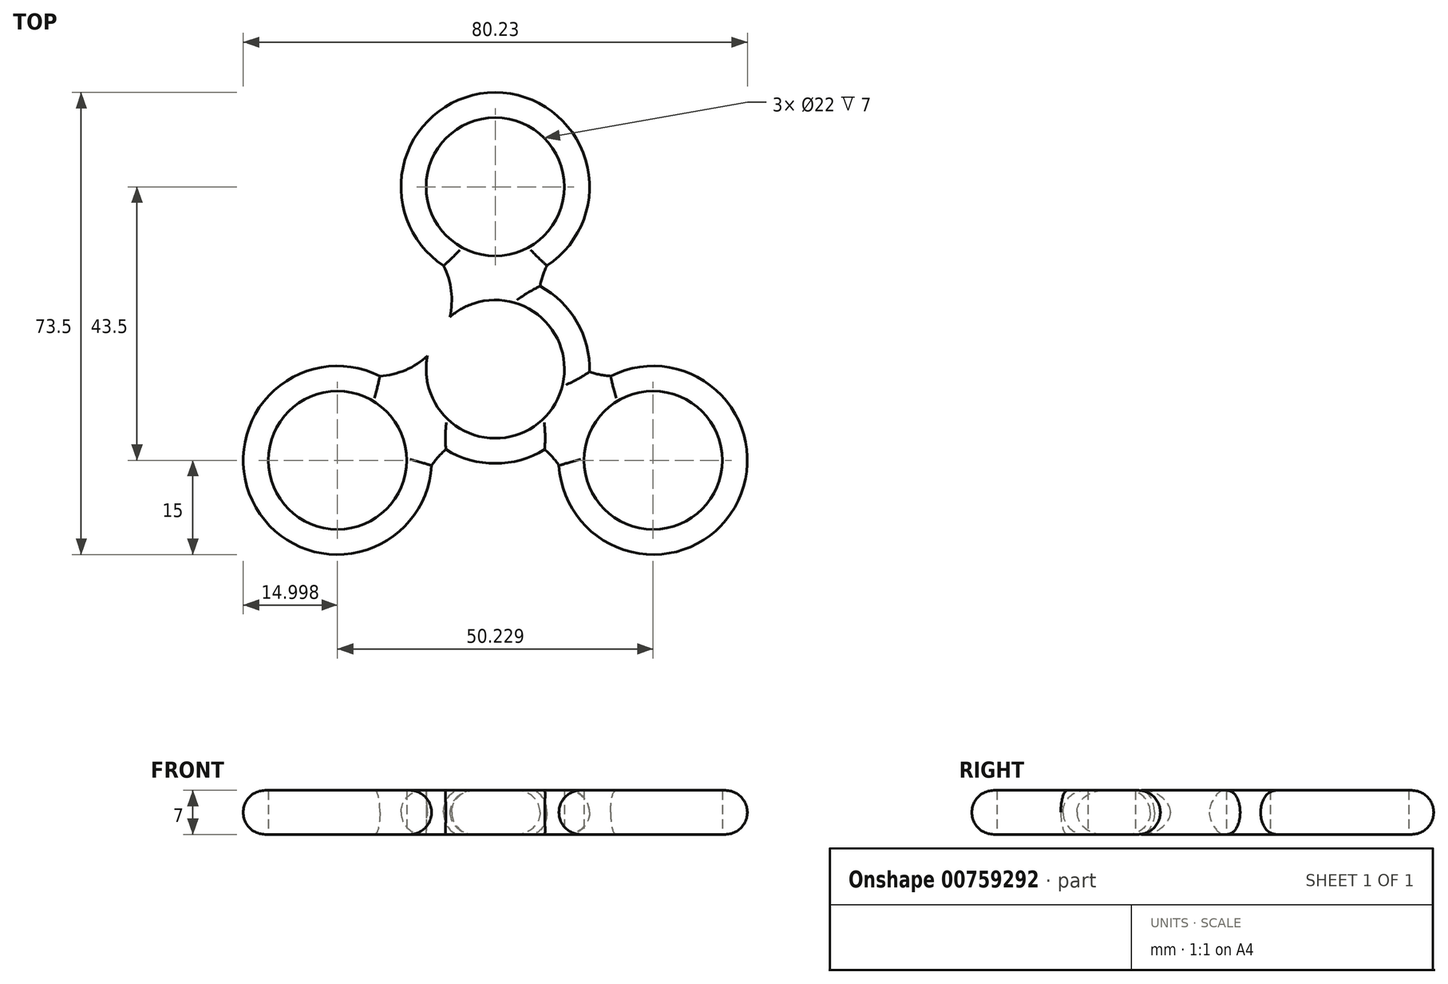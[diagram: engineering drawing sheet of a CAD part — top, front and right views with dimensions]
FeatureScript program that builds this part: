
annotation { "Feature Type Name" : "Feature", "Feature Type Description" : "" }
export const myFeature = defineFeature(function(context is Context, id is Id, definition is map)
    precondition{}
    {
        {
            var Q0;
            Q0=qCreatedBy(makeId("Top.planeOp"),FACE);
            var sketch = newSketch(context, id + "F0", { "sketchPlane" : qUnion([Q0])});
            skCircle(sketch, "E0", {"center": v(-46.13, 29) * mm, "radius": 15 * mm});
            skLineSegment(sketch, "E1", {"start": v(-46.13, 29) * mm, "end": v(-46.13, 0) * mm});
            skCircle(sketch, "E2.1.0", {"center": v(-71.24, -14.5) * mm, "radius": 15 * mm});
            skLineSegment(sketch, "E2.1.1", {"start": v(-71.24, -14.5) * mm, "end": v(-46.13, 0) * mm});
            skCircle(sketch, "E2.2.0", {"center": v(-21.01, -14.5) * mm, "radius": 15 * mm});
            skLineSegment(sketch, "E2.2.1", {"start": v(-21.01, -14.5) * mm, "end": v(-46.13, 0) * mm});
            skPoint(sketch, "E2.center", {"position": v(-46.13, 0) * mm});
            skLineSegment(sketch, "E3", {"start": v(-46.13, 29) * mm, "end": v(-59.12, 36.5) * mm});
            skLineSegment(sketch, "E4", {"start": v(-71.24, -14.5) * mm, "end": v(-84.23, -7) * mm});
            skPoint(sketch, "E5", {"position": v(-59.12, 21.5) * mm});
            skPoint(sketch, "E6", {"position": v(-71.24, 0.5) * mm});
            skPoint(sketch, "E7.1.0", {"position": v(-58.25, -22) * mm});
            skPoint(sketch, "E7.1.1", {"position": v(-34, -22) * mm});
            skPoint(sketch, "E7.2.0", {"position": v(-21.01, 0.5) * mm});
            skPoint(sketch, "E7.2.1", {"position": v(-33.14, 21.5) * mm});
            skArc(sketch, "E8", {"start": v(-71.24, 0.5) * mm, "mid": v(-54.68, 4.94) * mm, "end": v(-59.12, 21.5) * mm});
            skArc(sketch, "E9.1.0", {"start": v(-34, -22) * mm, "mid": v(-46.13, -9.88) * mm, "end": v(-58.25, -22) * mm});
            skArc(sketch, "E9.2.0", {"start": v(-33.14, 21.5) * mm, "mid": v(-37.57, 4.94) * mm, "end": v(-21.01, 0.5) * mm});
            skCircle(sketch, "E10", {"center": v(-46.13, 0) * mm, "radius": 15 * mm});
            skCircle(sketch, "E11", {"center": v(-46.13, 29) * mm, "radius": 11 * mm});
            skCircle(sketch, "E12", {"center": v(-71.24, -14.5) * mm, "radius": 11 * mm});
            skCircle(sketch, "E13", {"center": v(-21.01, -14.5) * mm, "radius": 11 * mm});
            skCircle(sketch, "E14", {"center": v(-46.13, 0) * mm, "radius": 11 * mm});
            skSolve(sketch);
        }
        {
            var Q0;
            {var subQ1=sQuery(id+"F0.wireOp",EDGE,"E0");var subQ10=sQuery(id+"F0.wireOp",EDGE,"E9.2.0");var subQ12=makeQuery(id+"F0.imprint","INTERSECT",VERTEX,{"disambiguationData":[OD(1.0)],"derivedFrom":[subQ1,subQ10]});Q0=makeQuery(id+"F0.imprint","IMPRINT",FACE,{"disambiguationData":[TD([[makeQuery(id+"F0.imprint","IMPRINT",EDGE,{"disambiguationData":[TD([[subQ12,1.0]])],"derivedFrom":subQ1}),1.0]])]});}
            var Q1;
            {var subQ0=sQuery(id+"F0.wireOp",EDGE,"E8");var subQ1=sQuery(id+"F0.wireOp",EDGE,"E0");var subQ2=makeQuery(id+"F0.imprint","INTERSECT",VERTEX,{"disambiguationData":[OD(0.0)],"derivedFrom":[subQ1,subQ0]});Q1=makeQuery(id+"F0.imprint","IMPRINT",FACE,{"disambiguationData":[TD([[makeQuery(id+"F0.imprint","IMPRINT",EDGE,{"disambiguationData":[TD([[subQ2,-1.0]])],"derivedFrom":subQ1}),1.0]])]});}
            var Q2;
            {var subQ0=sQuery(id+"F0.wireOp",EDGE,"E9.2.0");var subQ1=sQuery(id+"F0.wireOp",EDGE,"E0");var subQ2=makeQuery(id+"F0.imprint","INTERSECT",VERTEX,{"disambiguationData":[OD(0.0)],"derivedFrom":[subQ1,subQ0]});Q2=makeQuery(id+"F0.imprint","IMPRINT",FACE,{"disambiguationData":[TD([[makeQuery(id+"F0.imprint","IMPRINT",EDGE,{"disambiguationData":[TD([[subQ2,1.0]])],"derivedFrom":subQ1}),1.0]])]});}
            var Q3;
            {var subQ0=sQuery(id+"F0.wireOp",EDGE,"E1");var subQ1=sQuery(id+"F0.wireOp",EDGE,"E0");var subQ2=makeQuery(id+"F0.imprint","INTERSECT",VERTEX,{"derivedFrom":[subQ1,subQ0]});Q3=makeQuery(id+"F0.imprint","IMPRINT",FACE,{"disambiguationData":[TD([[makeQuery(id+"F0.imprint","IMPRINT",EDGE,{"disambiguationData":[TD([[subQ2,-1.0]])],"derivedFrom":subQ1}),1.0]])]});}
            var Q4;
            {var subQ0=sQuery(id+"F0.wireOp",EDGE,"E3");var subQ1=sQuery(id+"F0.wireOp",EDGE,"E0");var subQ2=makeQuery(id+"F0.imprint","INTERSECT",VERTEX,{"derivedFrom":[subQ1,subQ0]});Q4=makeQuery(id+"F0.imprint","IMPRINT",FACE,{"disambiguationData":[TD([[makeQuery(id+"F0.imprint","IMPRINT",EDGE,{"disambiguationData":[TD([[subQ2,-1.0]])],"derivedFrom":subQ1}),1.0]])]});}
            var Q5;
            {var subQ0=sQuery(id+"F0.wireOp",EDGE,"E10");var subQ1=sQuery(id+"F0.wireOp",EDGE,"E0");var subQ2=makeQuery(id+"F0.imprint","INTERSECT",VERTEX,{"disambiguationData":[OD(0.0)],"derivedFrom":[subQ1,subQ0]});Q5=makeQuery(id+"F0.imprint","IMPRINT",FACE,{"disambiguationData":[TD([[makeQuery(id+"F0.imprint","IMPRINT",EDGE,{"disambiguationData":[TD([[subQ2,-1.0]])],"derivedFrom":subQ1}),1.0]])]});}
            var Q6;
            {var subQ3=sQuery(id+"F0.wireOp",EDGE,"E10");var subQ7=sQuery(id+"F0.wireOp",EDGE,"E0");var subQ11=makeQuery(id+"F0.imprint","INTERSECT",VERTEX,{"disambiguationData":[OD(0.0)],"derivedFrom":[subQ7,subQ3]});Q6=makeQuery(id+"F0.imprint","IMPRINT",FACE,{"disambiguationData":[TD([[makeQuery(id+"F0.imprint","IMPRINT",EDGE,{"disambiguationData":[TD([[subQ11,-1.0]])],"derivedFrom":subQ7}),-1.0]])]});}
            var Q7;
            {var subQ1=sQuery(id+"F0.wireOp",EDGE,"E1");var subQ9=sQuery(id+"F0.wireOp",EDGE,"E0");var subQ10=makeQuery(id+"F0.imprint","INTERSECT",VERTEX,{"derivedFrom":[subQ9,subQ1]});Q7=makeQuery(id+"F0.imprint","IMPRINT",FACE,{"disambiguationData":[TD([[makeQuery(id+"F0.imprint","IMPRINT",EDGE,{"disambiguationData":[TD([[subQ10,-1.0]])],"derivedFrom":subQ9}),-1.0]])]});}
            var Q8;
            {var subQ0=sQuery(id+"F0.wireOp",EDGE,"E10");var subQ1=sQuery(id+"F0.wireOp",EDGE,"E9.2.0");var subQ2=makeQuery(id+"F0.imprint","INTERSECT",VERTEX,{"disambiguationData":[OD(0.0)],"derivedFrom":[subQ1,subQ0]});Q8=makeQuery(id+"F0.imprint","IMPRINT",FACE,{"disambiguationData":[TD([[makeQuery(id+"F0.imprint","IMPRINT",EDGE,{"disambiguationData":[TD([[subQ2,-1.0]])],"derivedFrom":subQ1}),1.0]])]});}
            var Q9;
            {var subQ0=sQuery(id+"F0.wireOp",EDGE,"E9.2.0");var subQ1=sQuery(id+"F0.wireOp",EDGE,"E0");var subQ2=makeQuery(id+"F0.imprint","INTERSECT",VERTEX,{"disambiguationData":[OD(1.0)],"derivedFrom":[subQ1,subQ0]});Q9=makeQuery(id+"F0.imprint","IMPRINT",FACE,{"disambiguationData":[TD([[makeQuery(id+"F0.imprint","IMPRINT",EDGE,{"disambiguationData":[TD([[subQ2,1.0]])],"derivedFrom":subQ1}),-1.0]])]});}
            var Q10;
            {var subQ0=sQuery(id+"F0.wireOp",EDGE,"E10");var subQ1=sQuery(id+"F0.wireOp",EDGE,"E8");var subQ2=makeQuery(id+"F0.imprint","INTERSECT",VERTEX,{"disambiguationData":[OD(0.0)],"derivedFrom":[subQ1,subQ0]});Q10=makeQuery(id+"F0.imprint","IMPRINT",FACE,{"disambiguationData":[TD([[makeQuery(id+"F0.imprint","IMPRINT",EDGE,{"disambiguationData":[TD([[subQ2,-1.0]])],"derivedFrom":subQ1}),1.0]])]});}
            var Q11;
            {var subQ0=sQuery(id+"F0.wireOp",EDGE,"E8");var subQ1=sQuery(id+"F0.wireOp",EDGE,"E0");var subQ2=makeQuery(id+"F0.imprint","INTERSECT",VERTEX,{"disambiguationData":[OD(1.0)],"derivedFrom":[subQ1,subQ0]});Q11=makeQuery(id+"F0.imprint","IMPRINT",FACE,{"disambiguationData":[TD([[makeQuery(id+"F0.imprint","IMPRINT",EDGE,{"disambiguationData":[TD([[subQ2,-1.0]])],"derivedFrom":subQ1}),-1.0]])]});}
            var Q12;
            {var subQ5=sQuery(id+"F0.wireOp",EDGE,"E10");var subQ9=sQuery(id+"F0.wireOp",EDGE,"E2.1.0");var subQ10=makeQuery(id+"F0.imprint","INTERSECT",VERTEX,{"disambiguationData":[OD(0.0)],"derivedFrom":[subQ9,subQ5]});Q12=makeQuery(id+"F0.imprint","IMPRINT",FACE,{"disambiguationData":[TD([[makeQuery(id+"F0.imprint","IMPRINT",EDGE,{"disambiguationData":[TD([[subQ10,-1.0]])],"derivedFrom":subQ9}),-1.0]])]});}
            var Q13;
            {var subQ0=sQuery(id+"F0.wireOp",EDGE,"E10");var subQ1=sQuery(id+"F0.wireOp",EDGE,"E9.1.0");var subQ2=makeQuery(id+"F0.imprint","INTERSECT",VERTEX,{"disambiguationData":[OD(0.0)],"derivedFrom":[subQ1,subQ0]});Q13=makeQuery(id+"F0.imprint","IMPRINT",FACE,{"disambiguationData":[TD([[makeQuery(id+"F0.imprint","IMPRINT",EDGE,{"disambiguationData":[TD([[subQ2,-1.0]])],"derivedFrom":subQ1}),1.0]])]});}
            var Q14;
            {var subQ0=sQuery(id+"F0.wireOp",EDGE,"E9.1.0");var subQ1=sQuery(id+"F0.wireOp",EDGE,"E2.1.0");var subQ2=makeQuery(id+"F0.imprint","INTERSECT",VERTEX,{"disambiguationData":[OD(1.0)],"derivedFrom":[subQ1,subQ0]});Q14=makeQuery(id+"F0.imprint","IMPRINT",FACE,{"disambiguationData":[TD([[makeQuery(id+"F0.imprint","IMPRINT",EDGE,{"disambiguationData":[TD([[subQ2,-1.0]])],"derivedFrom":subQ1}),-1.0]])]});}
            var Q15;
            {var subQ0=sQuery(id+"F0.wireOp",EDGE,"E8");var subQ1=sQuery(id+"F0.wireOp",EDGE,"E2.1.0");var subQ2=makeQuery(id+"F0.imprint","INTERSECT",VERTEX,{"disambiguationData":[OD(0.0)],"derivedFrom":[subQ1,subQ0]});Q15=makeQuery(id+"F0.imprint","IMPRINT",FACE,{"disambiguationData":[TD([[makeQuery(id+"F0.imprint","IMPRINT",EDGE,{"disambiguationData":[TD([[subQ2,1.0]])],"derivedFrom":subQ1}),1.0]])]});}
            var Q16;
            {var subQ0=sQuery(id+"F0.wireOp",EDGE,"E8");var subQ1=sQuery(id+"F0.wireOp",EDGE,"E2.1.0");var subQ2=makeQuery(id+"F0.imprint","INTERSECT",VERTEX,{"disambiguationData":[OD(1.0)],"derivedFrom":[subQ1,subQ0]});Q16=makeQuery(id+"F0.imprint","IMPRINT",FACE,{"disambiguationData":[TD([[makeQuery(id+"F0.imprint","IMPRINT",EDGE,{"disambiguationData":[TD([[subQ2,1.0]])],"derivedFrom":subQ1}),-1.0]])]});}
            var Q17;
            {var subQ0=sQuery(id+"F0.wireOp",EDGE,"E4");var subQ1=sQuery(id+"F0.wireOp",EDGE,"E2.1.0");var subQ2=makeQuery(id+"F0.imprint","INTERSECT",VERTEX,{"derivedFrom":[subQ1,subQ0]});Q17=makeQuery(id+"F0.imprint","IMPRINT",FACE,{"disambiguationData":[TD([[makeQuery(id+"F0.imprint","IMPRINT",EDGE,{"disambiguationData":[TD([[subQ2,-1.0]])],"derivedFrom":subQ1}),1.0]])]});}
            var Q18;
            {var subQ0=sQuery(id+"F0.wireOp",EDGE,"E9.1.0");var subQ1=sQuery(id+"F0.wireOp",EDGE,"E2.1.0");var subQ2=makeQuery(id+"F0.imprint","INTERSECT",VERTEX,{"disambiguationData":[OD(0.0)],"derivedFrom":[subQ1,subQ0]});Q18=makeQuery(id+"F0.imprint","IMPRINT",FACE,{"disambiguationData":[TD([[makeQuery(id+"F0.imprint","IMPRINT",EDGE,{"disambiguationData":[TD([[subQ2,-1.0]])],"derivedFrom":subQ1}),1.0]])]});}
            var Q19;
            {var subQ0=sQuery(id+"F0.wireOp",EDGE,"E2.1.1");var subQ1=sQuery(id+"F0.wireOp",EDGE,"E2.1.0");var subQ2=makeQuery(id+"F0.imprint","INTERSECT",VERTEX,{"derivedFrom":[subQ1,subQ0]});Q19=makeQuery(id+"F0.imprint","IMPRINT",FACE,{"disambiguationData":[TD([[makeQuery(id+"F0.imprint","IMPRINT",EDGE,{"disambiguationData":[TD([[subQ2,-1.0]])],"derivedFrom":subQ1}),1.0]])]});}
            var Q20;
            {var subQ1=sQuery(id+"F0.wireOp",EDGE,"E2.1.0");var subQ10=sQuery(id+"F0.wireOp",EDGE,"E8");var subQ12=makeQuery(id+"F0.imprint","INTERSECT",VERTEX,{"disambiguationData":[OD(1.0)],"derivedFrom":[subQ1,subQ10]});Q20=makeQuery(id+"F0.imprint","IMPRINT",FACE,{"disambiguationData":[TD([[makeQuery(id+"F0.imprint","IMPRINT",EDGE,{"disambiguationData":[TD([[subQ12,1.0]])],"derivedFrom":subQ1}),1.0]])]});}
            var Q21;
            {var subQ0=sQuery(id+"F0.wireOp",EDGE,"E2.2.1");var subQ1=sQuery(id+"F0.wireOp",EDGE,"E2.2.0");var subQ2=makeQuery(id+"F0.imprint","INTERSECT",VERTEX,{"derivedFrom":[subQ1,subQ0]});Q21=makeQuery(id+"F0.imprint","IMPRINT",FACE,{"disambiguationData":[TD([[makeQuery(id+"F0.imprint","IMPRINT",EDGE,{"disambiguationData":[TD([[subQ2,-1.0]])],"derivedFrom":subQ1}),1.0]])]});}
            var Q22;
            Q22=makeQuery(id+"F0.imprint","IMPRINT",FACE,{"disambiguationData":[TD([[makeQuery(id+"F0.imprint","IMPRINT",EDGE,{"derivedFrom":sQuery(id+"F0.wireOp",EDGE,"E13")}),-1.0]])]});
            var Q23;
            {var subQ0=sQuery(id+"F0.wireOp",EDGE,"E10");var subQ1=sQuery(id+"F0.wireOp",EDGE,"E2.2.0");var subQ2=makeQuery(id+"F0.imprint","INTERSECT",VERTEX,{"disambiguationData":[OD(0.0)],"derivedFrom":[subQ1,subQ0]});Q23=makeQuery(id+"F0.imprint","IMPRINT",FACE,{"disambiguationData":[TD([[makeQuery(id+"F0.imprint","IMPRINT",EDGE,{"disambiguationData":[TD([[subQ2,-1.0]])],"derivedFrom":subQ1}),1.0]])]});}
            var Q24;
            {var subQ0=sQuery(id+"F0.wireOp",EDGE,"E9.1.0");var subQ1=sQuery(id+"F0.wireOp",EDGE,"E2.2.0");var subQ2=makeQuery(id+"F0.imprint","INTERSECT",VERTEX,{"disambiguationData":[OD(0.0)],"derivedFrom":[subQ1,subQ0]});Q24=makeQuery(id+"F0.imprint","IMPRINT",FACE,{"disambiguationData":[TD([[makeQuery(id+"F0.imprint","IMPRINT",EDGE,{"disambiguationData":[TD([[subQ2,1.0]])],"derivedFrom":subQ1}),1.0]])]});}
            var Q25;
            {var subQ0=sQuery(id+"F0.wireOp",EDGE,"E9.2.0");var subQ1=sQuery(id+"F0.wireOp",EDGE,"E2.2.0");var subQ2=makeQuery(id+"F0.imprint","INTERSECT",VERTEX,{"disambiguationData":[OD(0.0)],"derivedFrom":[subQ1,subQ0]});Q25=makeQuery(id+"F0.imprint","IMPRINT",FACE,{"disambiguationData":[TD([[makeQuery(id+"F0.imprint","IMPRINT",EDGE,{"disambiguationData":[TD([[subQ2,-1.0]])],"derivedFrom":subQ1}),1.0]])]});}
            var Q26;
            {var subQ0=sQuery(id+"F0.wireOp",EDGE,"E10");var subQ1=sQuery(id+"F0.wireOp",EDGE,"E2.1.0");var subQ2=makeQuery(id+"F0.imprint","INTERSECT",VERTEX,{"disambiguationData":[OD(0.0)],"derivedFrom":[subQ1,subQ0]});Q26=makeQuery(id+"F0.imprint","IMPRINT",FACE,{"disambiguationData":[TD([[makeQuery(id+"F0.imprint","IMPRINT",EDGE,{"disambiguationData":[TD([[subQ2,-1.0]])],"derivedFrom":subQ1}),1.0]])]});}
            var Q27;
            {var subQ0=sQuery(id+"F0.wireOp",EDGE,"E9.2.0");var subQ1=sQuery(id+"F0.wireOp",EDGE,"E2.2.0");var subQ2=makeQuery(id+"F0.imprint","INTERSECT",VERTEX,{"disambiguationData":[OD(1.0)],"derivedFrom":[subQ1,subQ0]});Q27=makeQuery(id+"F0.imprint","IMPRINT",FACE,{"disambiguationData":[TD([[makeQuery(id+"F0.imprint","IMPRINT",EDGE,{"disambiguationData":[TD([[subQ2,-1.0]])],"derivedFrom":subQ1}),-1.0]])]});}
            var Q28;
            {var subQ0=sQuery(id+"F0.wireOp",EDGE,"E9.1.0");var subQ1=sQuery(id+"F0.wireOp",EDGE,"E2.2.0");var subQ2=makeQuery(id+"F0.imprint","INTERSECT",VERTEX,{"disambiguationData":[OD(1.0)],"derivedFrom":[subQ1,subQ0]});Q28=makeQuery(id+"F0.imprint","IMPRINT",FACE,{"disambiguationData":[TD([[makeQuery(id+"F0.imprint","IMPRINT",EDGE,{"disambiguationData":[TD([[subQ2,1.0]])],"derivedFrom":subQ1}),-1.0]])]});}
            var Q29;
            {var subQ3=sQuery(id+"F0.wireOp",EDGE,"E2.1.0");var subQ5=sQuery(id+"F0.wireOp",EDGE,"E2.1.1");var subQ6=makeQuery(id+"F0.imprint","INTERSECT",VERTEX,{"derivedFrom":[subQ3,subQ5]});Q29=makeQuery(id+"F0.imprint","IMPRINT",FACE,{"disambiguationData":[TD([[makeQuery(id+"F0.imprint","IMPRINT",EDGE,{"disambiguationData":[TD([[subQ6,-1.0]])],"derivedFrom":subQ3}),-1.0]])]});}
            var Q30;
            {var subQ3=sQuery(id+"F0.wireOp",EDGE,"E2.2.0");var subQ7=sQuery(id+"F0.wireOp",EDGE,"E2.2.1");var subQ8=makeQuery(id+"F0.imprint","INTERSECT",VERTEX,{"derivedFrom":[subQ3,subQ7]});Q30=makeQuery(id+"F0.imprint","IMPRINT",FACE,{"disambiguationData":[TD([[makeQuery(id+"F0.imprint","IMPRINT",EDGE,{"disambiguationData":[TD([[subQ8,-1.0]])],"derivedFrom":subQ3}),-1.0]])]});}
            var Q31;
            {var subQ0=sQuery(id+"F0.wireOp",EDGE,"E10");var subQ3=sQuery(id+"F0.wireOp",EDGE,"E2.2.0");var subQ4=makeQuery(id+"F0.imprint","INTERSECT",VERTEX,{"disambiguationData":[OD(0.0)],"derivedFrom":[subQ3,subQ0]});Q31=makeQuery(id+"F0.imprint","IMPRINT",FACE,{"disambiguationData":[TD([[makeQuery(id+"F0.imprint","IMPRINT",EDGE,{"disambiguationData":[TD([[subQ4,-1.0]])],"derivedFrom":subQ3}),-1.0]])]});}
            extrude(context, id + "F1", {"entities" : qUnion([Q0, Q1, Q2, Q3, Q4, Q5, Q6, Q7, Q8, Q9, Q10, Q11, Q12, Q13, Q14, Q15, Q16, Q17, Q18, Q19, Q20, Q21, Q22, Q23, Q24, Q25, Q26, Q27, Q28, Q29, Q30, Q31]), "depth" : 7 * mm, "offsetDistance" : 25.4 * mm});
        }
        {
            var Q0;
            Q0=makeQuery(id+"F1.opExtrude","CAP_EDGE",EDGE,{"disambiguationData":[OSD([sQuery(id+"F0.wireOp",EDGE,"E0")])],"isStart":true});
            var Q1;
            {var subQ0=sQuery(id+"F0.wireOp",EDGE,"E9.2.0");Q1=makeQuery(id+"F1.opExtrude","CAP_EDGE",EDGE,{"disambiguationData":[OSD([subQ0]),TDD([makeQuery(id+"F0.imprint","IMPRINT",EDGE,{"disambiguationData":[TD([[makeQuery(id+"F0.imprint","INTERSECT",VERTEX,{"disambiguationData":[OD(1.0)],"derivedFrom":[sQuery(id+"F0.wireOp",EDGE,"E0"),subQ0]}),-1.0]])],"derivedFrom":subQ0})])],"isStart":true});}
            var Q2;
            {var subQ0=sQuery(id+"F0.wireOp",EDGE,"E10");var subQ1=sQuery(id+"F0.wireOp",EDGE,"E9.2.0");Q2=makeQuery(id+"F1.opExtrude","CAP_EDGE",EDGE,{"disambiguationData":[OSD([subQ0]),TDD([makeQuery(id+"F0.imprint","IMPRINT",EDGE,{"disambiguationData":[TD([[makeQuery(id+"F0.imprint","INTERSECT",VERTEX,{"disambiguationData":[OD(0.0)],"derivedFrom":[subQ1,subQ0]}),1.0]])],"derivedFrom":subQ0})])],"isStart":true});}
            var Q3;
            {var subQ0=sQuery(id+"F0.wireOp",EDGE,"E9.2.0");Q3=makeQuery(id+"F1.opExtrude","CAP_EDGE",EDGE,{"disambiguationData":[OSD([subQ0]),TDD([makeQuery(id+"F0.imprint","IMPRINT",EDGE,{"disambiguationData":[TD([[makeQuery(id+"F0.imprint","INTERSECT",VERTEX,{"disambiguationData":[OD(1.0)],"derivedFrom":[sQuery(id+"F0.wireOp",EDGE,"E2.2.0"),subQ0]}),1.0]])],"derivedFrom":subQ0})])],"isStart":true});}
            var Q4;
            Q4=makeQuery(id+"F1.opExtrude","CAP_EDGE",EDGE,{"disambiguationData":[OSD([sQuery(id+"F0.wireOp",EDGE,"E2.2.0")])],"isStart":true});
            var Q5;
            {var subQ0=sQuery(id+"F0.wireOp",EDGE,"E9.1.0");Q5=makeQuery(id+"F1.opExtrude","CAP_EDGE",EDGE,{"disambiguationData":[OSD([subQ0]),TDD([makeQuery(id+"F0.imprint","IMPRINT",EDGE,{"disambiguationData":[TD([[makeQuery(id+"F0.imprint","INTERSECT",VERTEX,{"disambiguationData":[OD(1.0)],"derivedFrom":[sQuery(id+"F0.wireOp",EDGE,"E2.2.0"),subQ0]}),-1.0]])],"derivedFrom":subQ0})])],"isStart":true});}
            var Q6;
            {var subQ0=sQuery(id+"F0.wireOp",EDGE,"E10");var subQ1=sQuery(id+"F0.wireOp",EDGE,"E9.1.0");Q6=makeQuery(id+"F1.opExtrude","CAP_EDGE",EDGE,{"disambiguationData":[OSD([subQ0]),TDD([makeQuery(id+"F0.imprint","IMPRINT",EDGE,{"disambiguationData":[TD([[makeQuery(id+"F0.imprint","INTERSECT",VERTEX,{"disambiguationData":[OD(0.0)],"derivedFrom":[subQ1,subQ0]}),1.0]])],"derivedFrom":subQ0})])],"isStart":true});}
            var Q7;
            {var subQ0=sQuery(id+"F0.wireOp",EDGE,"E9.1.0");Q7=makeQuery(id+"F1.opExtrude","CAP_EDGE",EDGE,{"disambiguationData":[OSD([subQ0]),TDD([makeQuery(id+"F0.imprint","IMPRINT",EDGE,{"disambiguationData":[TD([[makeQuery(id+"F0.imprint","INTERSECT",VERTEX,{"disambiguationData":[OD(1.0)],"derivedFrom":[sQuery(id+"F0.wireOp",EDGE,"E2.1.0"),subQ0]}),1.0]])],"derivedFrom":subQ0})])],"isStart":true});}
            var Q8;
            Q8=makeQuery(id+"F1.opExtrude","CAP_EDGE",EDGE,{"disambiguationData":[OSD([sQuery(id+"F0.wireOp",EDGE,"E2.1.0")])],"isStart":true});
            var Q9;
            {var subQ0=sQuery(id+"F0.wireOp",EDGE,"E8");Q9=makeQuery(id+"F1.opExtrude","CAP_EDGE",EDGE,{"disambiguationData":[OSD([subQ0]),TDD([makeQuery(id+"F0.imprint","IMPRINT",EDGE,{"disambiguationData":[TD([[makeQuery(id+"F0.imprint","INTERSECT",VERTEX,{"disambiguationData":[OD(1.0)],"derivedFrom":[sQuery(id+"F0.wireOp",EDGE,"E2.1.0"),subQ0]}),-1.0]])],"derivedFrom":subQ0})])],"isStart":true});}
            var Q10;
            {var subQ0=sQuery(id+"F0.wireOp",EDGE,"E10");var subQ1=sQuery(id+"F0.wireOp",EDGE,"E8");Q10=makeQuery(id+"F1.opExtrude","CAP_EDGE",EDGE,{"disambiguationData":[OSD([subQ0]),TDD([makeQuery(id+"F0.imprint","IMPRINT",EDGE,{"disambiguationData":[TD([[makeQuery(id+"F0.imprint","INTERSECT",VERTEX,{"disambiguationData":[OD(0.0)],"derivedFrom":[subQ1,subQ0]}),1.0]])],"derivedFrom":subQ0})])],"isStart":true});}
            var Q11;
            {var subQ0=sQuery(id+"F0.wireOp",EDGE,"E8");Q11=makeQuery(id+"F1.opExtrude","CAP_EDGE",EDGE,{"disambiguationData":[OSD([subQ0]),TDD([makeQuery(id+"F0.imprint","IMPRINT",EDGE,{"disambiguationData":[TD([[makeQuery(id+"F0.imprint","INTERSECT",VERTEX,{"disambiguationData":[OD(1.0)],"derivedFrom":[sQuery(id+"F0.wireOp",EDGE,"E0"),subQ0]}),1.0]])],"derivedFrom":subQ0})])],"isStart":true});}
            var Q12;
            Q12=makeQuery(id+"F1.opExtrude","CAP_EDGE",EDGE,{"disambiguationData":[OSD([sQuery(id+"F0.wireOp",EDGE,"E2.2.0")])],"isStart":false});
            var Q13;
            {var subQ0=sQuery(id+"F0.wireOp",EDGE,"E9.2.0");Q13=makeQuery(id+"F1.opExtrude","CAP_EDGE",EDGE,{"disambiguationData":[OSD([subQ0]),TDD([makeQuery(id+"F0.imprint","IMPRINT",EDGE,{"disambiguationData":[TD([[makeQuery(id+"F0.imprint","INTERSECT",VERTEX,{"disambiguationData":[OD(1.0)],"derivedFrom":[sQuery(id+"F0.wireOp",EDGE,"E2.2.0"),subQ0]}),1.0]])],"derivedFrom":subQ0})])],"isStart":false});}
            var Q14;
            {var subQ0=sQuery(id+"F0.wireOp",EDGE,"E10");var subQ1=sQuery(id+"F0.wireOp",EDGE,"E9.2.0");Q14=makeQuery(id+"F1.opExtrude","CAP_EDGE",EDGE,{"disambiguationData":[OSD([subQ0]),TDD([makeQuery(id+"F0.imprint","IMPRINT",EDGE,{"disambiguationData":[TD([[makeQuery(id+"F0.imprint","INTERSECT",VERTEX,{"disambiguationData":[OD(0.0)],"derivedFrom":[subQ1,subQ0]}),1.0]])],"derivedFrom":subQ0})])],"isStart":false});}
            var Q15;
            {var subQ0=sQuery(id+"F0.wireOp",EDGE,"E9.2.0");Q15=makeQuery(id+"F1.opExtrude","CAP_EDGE",EDGE,{"disambiguationData":[OSD([subQ0]),TDD([makeQuery(id+"F0.imprint","IMPRINT",EDGE,{"disambiguationData":[TD([[makeQuery(id+"F0.imprint","INTERSECT",VERTEX,{"disambiguationData":[OD(1.0)],"derivedFrom":[sQuery(id+"F0.wireOp",EDGE,"E0"),subQ0]}),-1.0]])],"derivedFrom":subQ0})])],"isStart":false});}
            var Q16;
            Q16=makeQuery(id+"F1.opExtrude","CAP_EDGE",EDGE,{"disambiguationData":[OSD([sQuery(id+"F0.wireOp",EDGE,"E0")])],"isStart":false});
            var Q17;
            {var subQ0=sQuery(id+"F0.wireOp",EDGE,"E8");Q17=makeQuery(id+"F1.opExtrude","CAP_EDGE",EDGE,{"disambiguationData":[OSD([subQ0]),TDD([makeQuery(id+"F0.imprint","IMPRINT",EDGE,{"disambiguationData":[TD([[makeQuery(id+"F0.imprint","INTERSECT",VERTEX,{"disambiguationData":[OD(1.0)],"derivedFrom":[sQuery(id+"F0.wireOp",EDGE,"E0"),subQ0]}),1.0]])],"derivedFrom":subQ0})])],"isStart":false});}
            var Q18;
            {var subQ0=sQuery(id+"F0.wireOp",EDGE,"E10");var subQ1=sQuery(id+"F0.wireOp",EDGE,"E8");Q18=makeQuery(id+"F1.opExtrude","CAP_EDGE",EDGE,{"disambiguationData":[OSD([subQ0]),TDD([makeQuery(id+"F0.imprint","IMPRINT",EDGE,{"disambiguationData":[TD([[makeQuery(id+"F0.imprint","INTERSECT",VERTEX,{"disambiguationData":[OD(0.0)],"derivedFrom":[subQ1,subQ0]}),1.0]])],"derivedFrom":subQ0})])],"isStart":false});}
            var Q19;
            {var subQ0=sQuery(id+"F0.wireOp",EDGE,"E8");Q19=makeQuery(id+"F1.opExtrude","CAP_EDGE",EDGE,{"disambiguationData":[OSD([subQ0]),TDD([makeQuery(id+"F0.imprint","IMPRINT",EDGE,{"disambiguationData":[TD([[makeQuery(id+"F0.imprint","INTERSECT",VERTEX,{"disambiguationData":[OD(1.0)],"derivedFrom":[sQuery(id+"F0.wireOp",EDGE,"E2.1.0"),subQ0]}),-1.0]])],"derivedFrom":subQ0})])],"isStart":false});}
            var Q20;
            Q20=makeQuery(id+"F1.opExtrude","CAP_EDGE",EDGE,{"disambiguationData":[OSD([sQuery(id+"F0.wireOp",EDGE,"E2.1.0")])],"isStart":false});
            var Q21;
            {var subQ0=sQuery(id+"F0.wireOp",EDGE,"E9.1.0");Q21=makeQuery(id+"F1.opExtrude","CAP_EDGE",EDGE,{"disambiguationData":[OSD([subQ0]),TDD([makeQuery(id+"F0.imprint","IMPRINT",EDGE,{"disambiguationData":[TD([[makeQuery(id+"F0.imprint","INTERSECT",VERTEX,{"disambiguationData":[OD(1.0)],"derivedFrom":[sQuery(id+"F0.wireOp",EDGE,"E2.1.0"),subQ0]}),1.0]])],"derivedFrom":subQ0})])],"isStart":false});}
            var Q22;
            {var subQ0=sQuery(id+"F0.wireOp",EDGE,"E10");var subQ1=sQuery(id+"F0.wireOp",EDGE,"E9.1.0");Q22=makeQuery(id+"F1.opExtrude","CAP_EDGE",EDGE,{"disambiguationData":[OSD([subQ0]),TDD([makeQuery(id+"F0.imprint","IMPRINT",EDGE,{"disambiguationData":[TD([[makeQuery(id+"F0.imprint","INTERSECT",VERTEX,{"disambiguationData":[OD(0.0)],"derivedFrom":[subQ1,subQ0]}),1.0]])],"derivedFrom":subQ0})])],"isStart":false});}
            var Q23;
            {var subQ0=sQuery(id+"F0.wireOp",EDGE,"E9.1.0");Q23=makeQuery(id+"F1.opExtrude","CAP_EDGE",EDGE,{"disambiguationData":[OSD([subQ0]),TDD([makeQuery(id+"F0.imprint","IMPRINT",EDGE,{"disambiguationData":[TD([[makeQuery(id+"F0.imprint","INTERSECT",VERTEX,{"disambiguationData":[OD(1.0)],"derivedFrom":[sQuery(id+"F0.wireOp",EDGE,"E2.2.0"),subQ0]}),-1.0]])],"derivedFrom":subQ0})])],"isStart":false});}
            fillet(context, id + "F2", {"entities" : qUnion([Q0, Q1, Q2, Q3, Q4, Q5, Q6, Q7, Q8, Q9, Q10, Q11, Q12, Q13, Q14, Q15, Q16, Q17, Q18, Q19, Q20, Q21, Q22, Q23]), "radius" : 3.5 * mm, "tangentPropagation" : true, "allowEdgeOverflow" : false});
        }
    });
